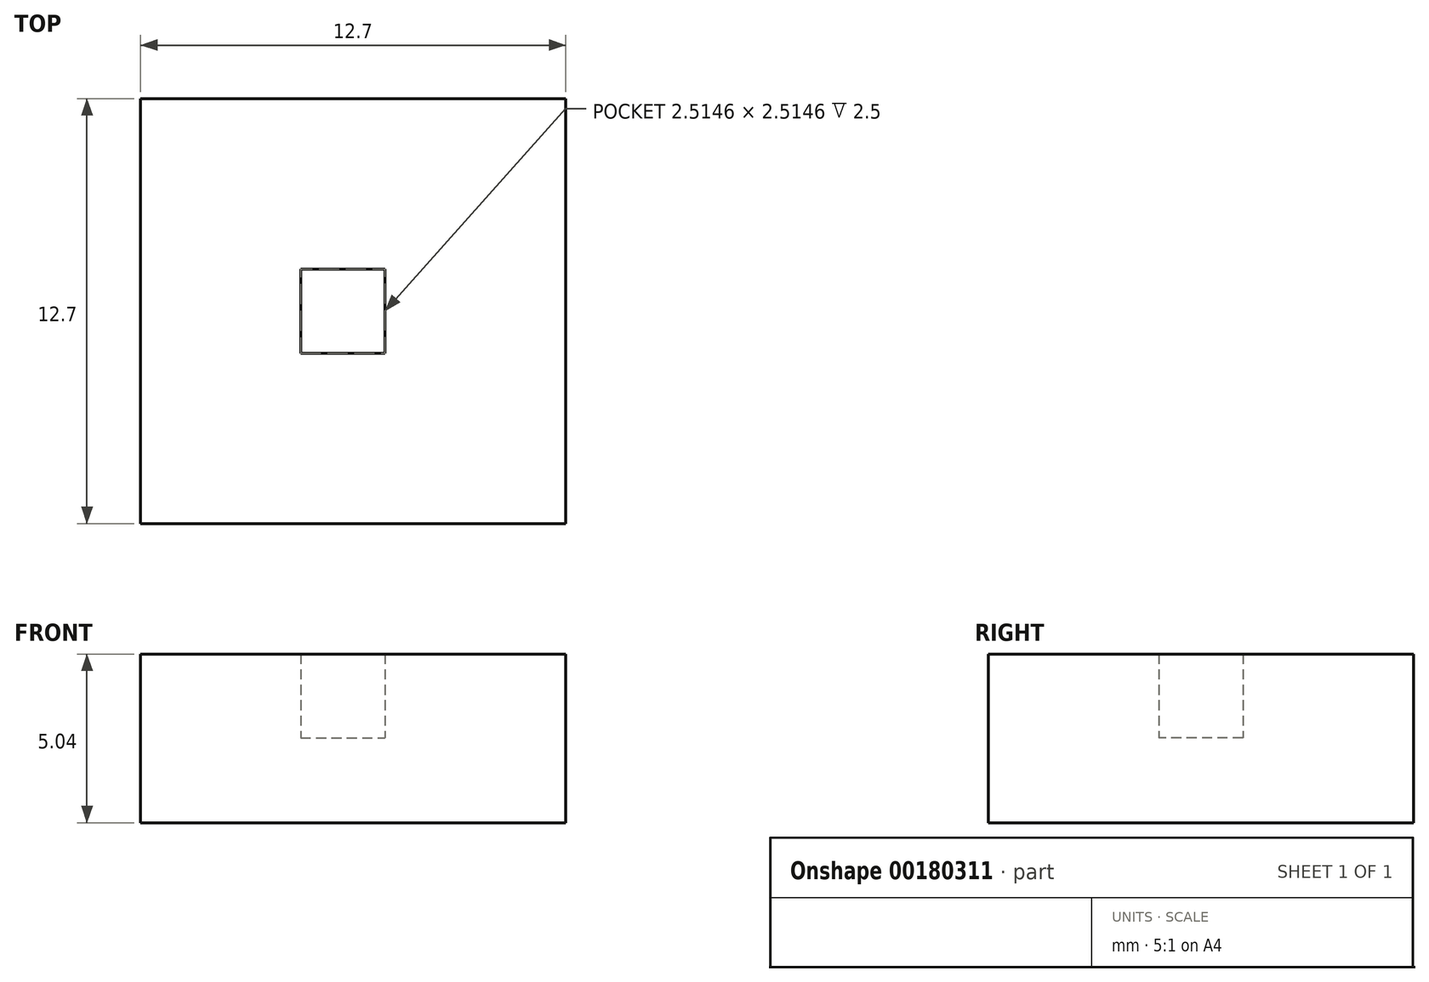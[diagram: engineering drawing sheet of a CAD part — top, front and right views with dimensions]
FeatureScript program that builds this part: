
annotation { "Feature Type Name" : "Feature", "Feature Type Description" : "" }
export const myFeature = defineFeature(function(context is Context, id is Id, definition is map)
    precondition{}
    {
        {
            var Q0;
            Q0=qCreatedBy(makeId("Top.planeOp"),FACE);
            var sketch = newSketch(context, id + "F0", { "sketchPlane" : qUnion([Q0])});
            skLineSegment(sketch, "E0.bottom", {"start": v(-61.86, 37.3) * mm, "end": v(-49.16, 37.3) * mm});
            skLineSegment(sketch, "E0.top", {"start": v(-61.86, 24.6) * mm, "end": v(-49.16, 24.6) * mm});
            skLineSegment(sketch, "E0.left", {"start": v(-61.86, 37.3) * mm, "end": v(-61.86, 24.6) * mm});
            skLineSegment(sketch, "E0.right", {"start": v(-49.16, 37.3) * mm, "end": v(-49.16, 24.6) * mm});
            skSolve(sketch);
        }
        {
            var Q0;
            Q0=makeQuery(id+"F0.imprint","IMPRINT",FACE,{"disambiguationData":[TD([[makeQuery(id+"F0.imprint","IMPRINT",EDGE,{"derivedFrom":sQuery(id+"F0.wireOp",EDGE,"E0.bottom")}),-1.0]])]});
            extrude(context, id + "F1", {"entities" : qUnion([Q0]), "oppositeDirection" : true, "depth" : 2.54 * mm});
        }
        {
            var Q0;
            Q0=makeQuery(id+"F1.opExtrude","CAP_FACE",FACE,{"disambiguationData":[OSD([sQuery(id+"F0.wireOp",EDGE,"E0.bottom"),sQuery(id+"F0.wireOp",EDGE,"E0.top"),sQuery(id+"F0.wireOp",EDGE,"E0.left"),sQuery(id+"F0.wireOp",EDGE,"E0.right")])],"isStart":true});
            var sketch = newSketch(context, id + "F2", { "sketchPlane" : qUnion([Q0])});
            skLineSegment(sketch, "E1.bottom", {"start": v(-57.08, 32.2) * mm, "end": v(-54.56, 32.2) * mm});
            skLineSegment(sketch, "E1.top", {"start": v(-57.08, 29.7) * mm, "end": v(-54.56, 29.7) * mm});
            skLineSegment(sketch, "E1.left", {"start": v(-57.08, 32.2) * mm, "end": v(-57.08, 29.7) * mm});
            skLineSegment(sketch, "E1.right", {"start": v(-54.56, 32.2) * mm, "end": v(-54.56, 29.7) * mm});
            skSolve(sketch);
        }
        {
            var Q0;
            Q0=makeQuery(id+"F2.imprint","IMPRINT",FACE,{"disambiguationData":[TD([[makeQuery(id+"F2.imprint","IMPRINT",EDGE,{"derivedFrom":sQuery(id+"F2.wireOp",EDGE,"E1.bottom")}),1.0]])]});
            extrude(context, id + "F3", {"entities" : qUnion([Q0]), "operationType" : NewBodyOperationType.ADD, "depth" : 2.5 * mm});
        }
    });
